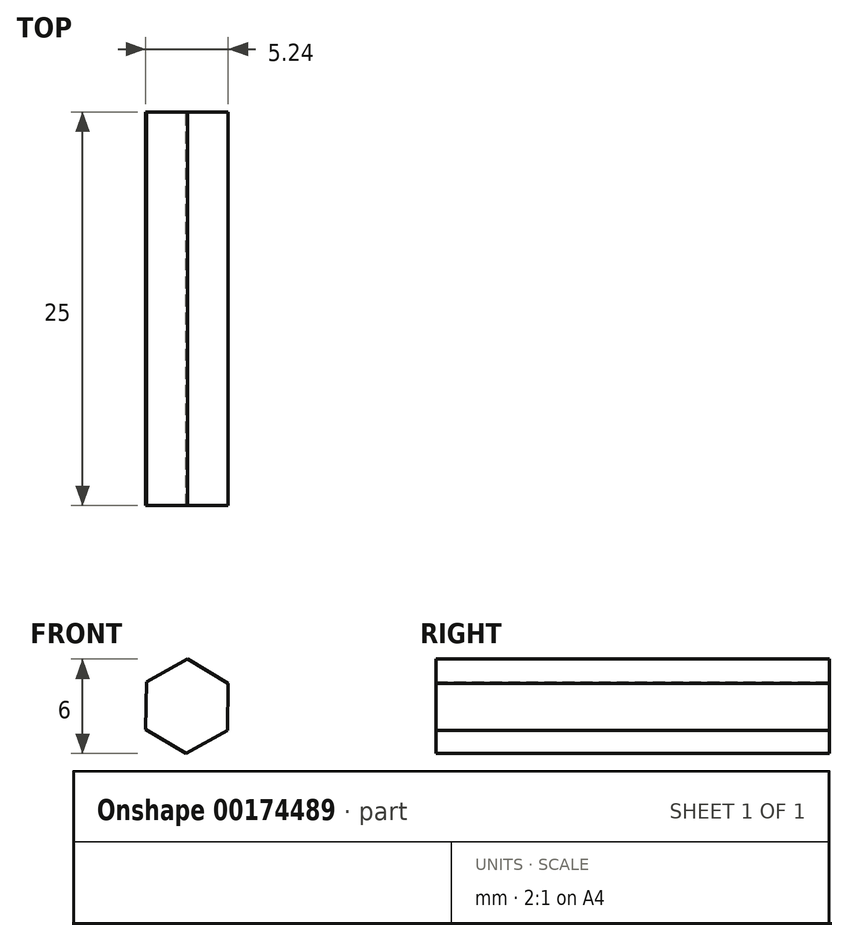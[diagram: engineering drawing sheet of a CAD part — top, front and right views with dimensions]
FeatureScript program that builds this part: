
annotation { "Feature Type Name" : "Feature", "Feature Type Description" : "" }
export const myFeature = defineFeature(function(context is Context, id is Id, definition is map)
    precondition{}
    {
        {
            var Q0;
            Q0=qCreatedBy(makeId("Front.planeOp"),FACE);
            var sketch = newSketch(context, id + "F0", { "sketchPlane" : qUnion([Q0])});
            skCircle(sketch, "E0.cCircle", {"center": v(0, 0) * mm, "radius": 2.6 * mm, "construction": true});
            skLineSegment(sketch, "E0.0", {"start": v(2.58, -1.54) * mm, "end": v(-0.04, -3) * mm});
            skLineSegment(sketch, "E0.1", {"start": v(-0.04, -3) * mm, "end": v(-2.62, -1.46) * mm});
            skLineSegment(sketch, "E0.2", {"start": v(-2.62, -1.46) * mm, "end": v(-2.58, 1.54) * mm});
            skLineSegment(sketch, "E0.3", {"start": v(-2.58, 1.54) * mm, "end": v(0.04, 3) * mm});
            skLineSegment(sketch, "E0.4", {"start": v(0.04, 3) * mm, "end": v(2.62, 1.46) * mm});
            skLineSegment(sketch, "E0.5", {"start": v(2.62, 1.46) * mm, "end": v(2.58, -1.54) * mm});
            skPoint(sketch, "E0.0.midPoint", {"position": v(1.27, -2.27) * mm});
            skSolve(sketch);
        }
        {
            var Q0;
            Q0=makeQuery(id+"F0.imprint","IMPRINT",FACE,{"disambiguationData":[TD([[makeQuery(id+"F0.imprint","IMPRINT",EDGE,{"derivedFrom":sQuery(id+"F0.wireOp",EDGE,"E0.0")}),-1.0]])]});
            extrude(context, id + "F1", {"entities" : qUnion([Q0]), "depth" : 25 * mm});
        }
    });
